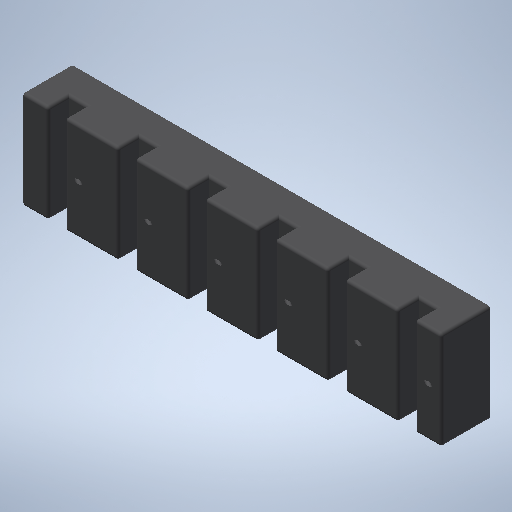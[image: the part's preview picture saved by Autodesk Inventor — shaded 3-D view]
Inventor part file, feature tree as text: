
AUTODESK INVENTOR PART (.ipt)
format: ipt  version: 2025.2 (Build 292293000, 293)  size: 376,832 bytes
history: native  units: in
note: dims shown in document units (in); Inventor stores cm internally (conversion verified against a paired STEP export)
features: extrude x5, plane x2, sketch x1, pattern_linear x1, fillet x1
ambient origin geometry x8: Origin, YZ Plane, XZ Plane, XY Plane, X Axis, Y Axis, Z Axis, Center Point
bodies: Solid1 (feature_tree)
feature tree (10):
  extrude  "Extrusion8"  Depth=2.7559in
  extrude  "Extrusion17"  Depth=5.9055in
  plane  "Work Plane11"
  sketch  "Sketch24"  dims[d0=11.811in d1=2.7559in d57=5.9055in d58=1.378in d85=1.1811in d86=0.5906in d102=1.378in d103=0.0in d175=0.5906in d176=0.4764in d178=0.0in d179=0.0in d180=0.3779in d181=0.126in d182=1.9685in d183=0.0in d188=0.1969in d189=0.1969in d192=0.5906in d193=0.0in d194=0.2461in d195=0.2461in d196=0.3937in d197=0.0in d200=0.7461in d204=9.8425in d205=4.9213in d206=0.1969in d207=2.3622in d209=1.9685in d210=0.2461in d211=0.0787in]
  plane  "Work Plane12"
  extrude  "Extrusion18"  Depth=1.378in
  extrude  "Extrusion20"  Depth=0.5906in
  extrude  "Extrusion21"  Depth=1.378in TaperAngle=0.0deg
  pattern_linear  "Rectangular Pattern5"  Spacing1=0.5906in  [1 undecoded]
  fillet  "Fillet6"  Radius=0.4764in
note: 1 required parameter value undecoded (feature->parameter linkage not recoverable at this tier; creation-order binding heuristic only, values carry confidence <= 0.55)
